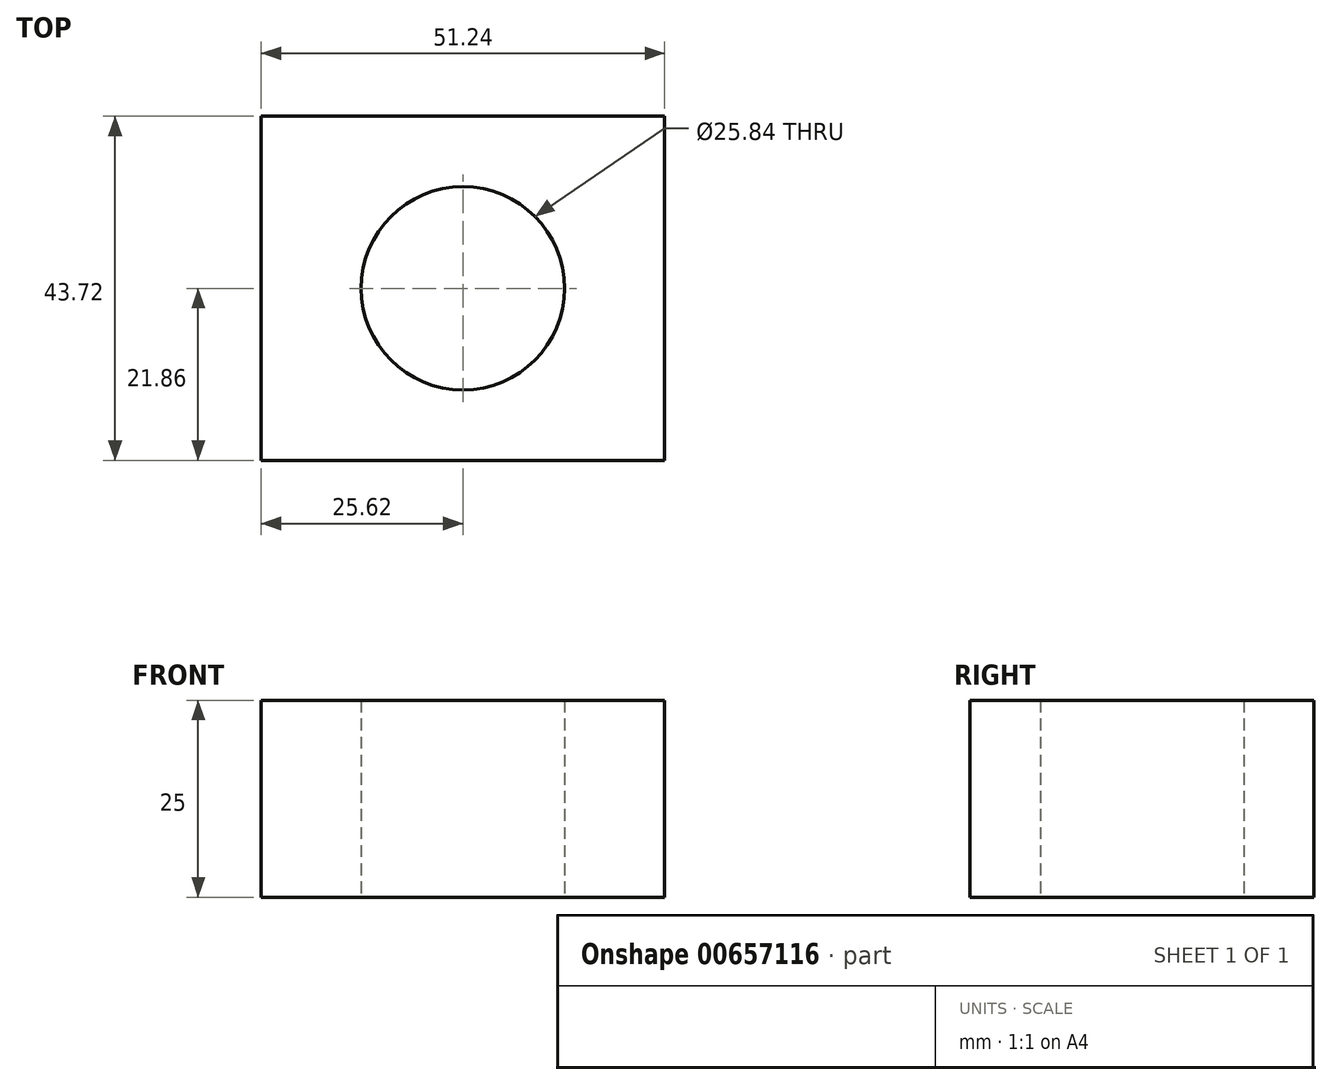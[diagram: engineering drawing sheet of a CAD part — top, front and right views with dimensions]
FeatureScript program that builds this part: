
annotation { "Feature Type Name" : "Feature", "Feature Type Description" : "" }
export const myFeature = defineFeature(function(context is Context, id is Id, definition is map)
    precondition{}
    {
        {
            var Q0;
            Q0=qCreatedBy(makeId("Top.planeOp"),FACE);
            var sketch = newSketch(context, id + "F0", { "sketchPlane" : qUnion([Q0])});
            skCircle(sketch, "E0", {"center": v(0, 0) * mm, "radius": 12.92 * mm});
            skLineSegment(sketch, "E1.bottom", {"start": v(25.62, 21.86) * mm, "end": v(-25.62, 21.86) * mm});
            skLineSegment(sketch, "E1.top", {"start": v(25.62, -21.86) * mm, "end": v(-25.62, -21.86) * mm});
            skLineSegment(sketch, "E1.left", {"start": v(-25.62, -21.86) * mm, "end": v(-25.62, 21.86) * mm});
            skLineSegment(sketch, "E1.right", {"start": v(25.62, -21.86) * mm, "end": v(25.62, 21.86) * mm});
            skSolve(sketch);
        }
        {
            var Q0;
            Q0 = qSketchRegion(id + "F0", true);
            extrude(context, id + "F1", {"entities" : qUnion([Q0]), "depth" : 25 * mm, "offsetDistance" : 25 * mm});
        }
    });
